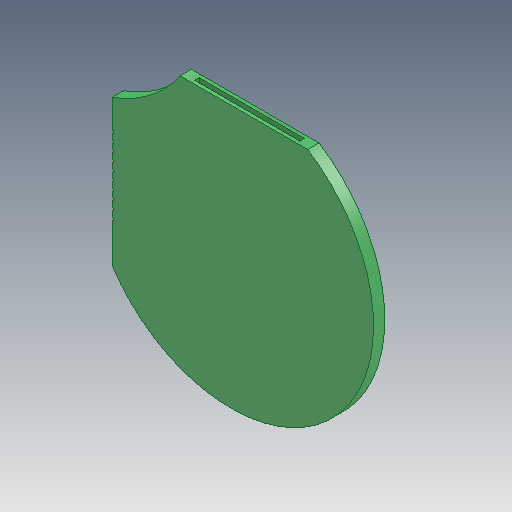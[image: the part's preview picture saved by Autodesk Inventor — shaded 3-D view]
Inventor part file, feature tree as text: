
AUTODESK INVENTOR PART (.ipt)
format: ipt  version: 2020.3 (Build 243373010, 373A)  size: 221,184 bytes
history: native  units: mm
features: extrude x6, sketch x5, pattern_linear x1, projected_geometry x1
ambient origin geometry x8: Origin, YZ Plane, XZ Plane, XY Plane, X Axis, Y Axis, Z Axis, Center Point
bodies: Solid1 (feature_tree)
feature tree (13):
  sketch  "Sketch1"  dims[d0=4.0mm d1=4.0mm d2=4.0mm d3=4.0mm d4=4.0mm d5=4.0mm d6=4.0mm d7=4.0mm d8=4.0mm d9=4.0mm d10=6.0mm d11=4.0mm d12=1.15mm d13=1.15mm d14=4.0mm d15=4.0mm d16=1.75mm d17=2.65mm d18=3.0mm d19=3.0mm d20=5.0mm d21=1.65mm d22=11.25mm d23=0.85mm d24=0.0mm]
  extrude  "Extrusion1"  Depth=0.85mm TaperAngle=0.0deg
  extrude  "Extrusion2"  Depth=1.5mm TaperAngle=0.0deg
  extrude  "Extrusion3"  Depth=2.0mm TaperAngle=0.0deg
  extrude  "Extrusion4"  Depth=18.5mm
  pattern_linear  "Rectangular Pattern1"  Spacing1=10.0mm  [1 undecoded]
  extrude  "Extrusion5"  Depth=1.5mm
  extrude  "Extrusion6"  Depth=0.45mm
  sketch  "Sketch3"  dims[d25=1.5mm d26=0.0mm d28=1.5mm d29=0.0mm]
  sketch  "Sketch4"  dims[d30=15.85mm d31=2.0mm d32=0.0mm]
  sketch  "Sketch5"  dims[d33=100.0mm d35=11.0mm d36=18.5mm]
  sketch  "Sketch6"  dims[d37=16.0mm d38=10.0mm d39=0.0mm d40=1.5mm d41=0.45mm d42=0.45mm d43=14.0mm d44=2.5mm d45=0.0mm]
  projected_geometry  "Projected Loop1"
note: 1 required parameter value undecoded (feature->parameter linkage not recoverable at this tier; creation-order binding heuristic only, values carry confidence <= 0.55)
